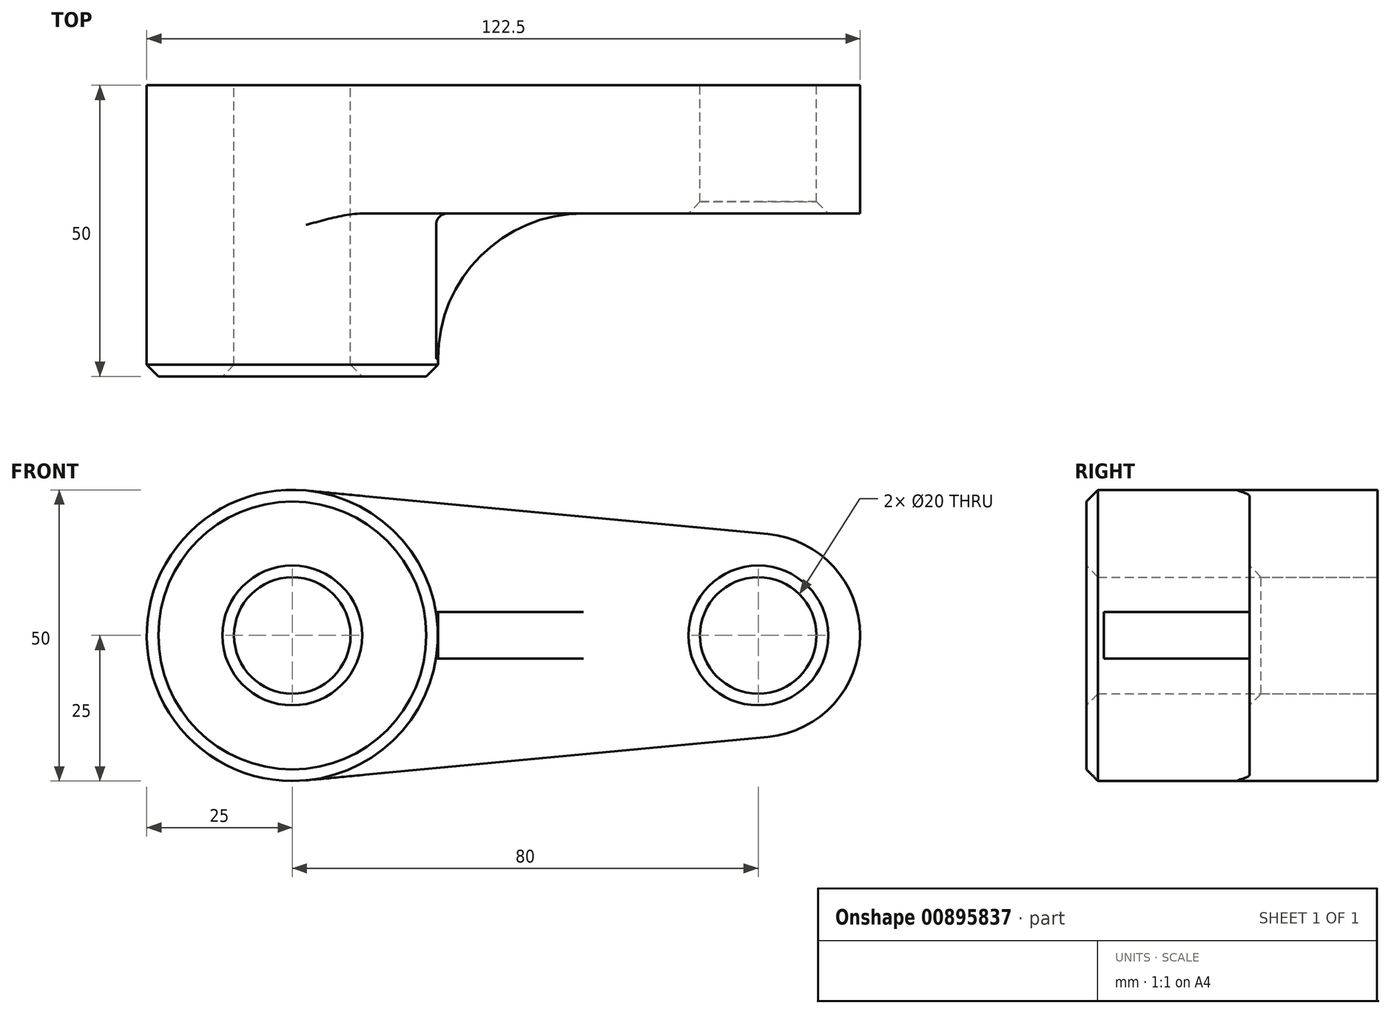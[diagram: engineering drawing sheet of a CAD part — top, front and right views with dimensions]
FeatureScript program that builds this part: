
annotation { "Feature Type Name" : "Feature", "Feature Type Description" : "" }
export const myFeature = defineFeature(function(context is Context, id is Id, definition is map)
    precondition{}
    {
        {
            var Q0;
            Q0=qCreatedBy(makeId("Front.planeOp"),FACE);
            var sketch = newSketch(context, id + "F0", { "sketchPlane" : qUnion([Q0])});
            skCircle(sketch, "E0", {"center": v(0, 0) * mm, "radius": 25 * mm});
            skCircle(sketch, "E1", {"center": v(80, 0) * mm, "radius": 17.5 * mm});
            skLineSegment(sketch, "E2", {"start": v(2.34, 24.89) * mm, "end": v(81.64, 17.42) * mm});
            skLineSegment(sketch, "E3", {"start": v(2.34, -24.89) * mm, "end": v(81.64, -17.42) * mm});
            skCircle(sketch, "E4", {"center": v(0, 0) * mm, "radius": 10 * mm});
            skCircle(sketch, "E5", {"center": v(80, 0) * mm, "radius": 10 * mm});
            skSolve(sketch);
        }
        {
            var Q0;
            Q0 = qSketchRegion(id + "F0", true);
            extrude(context, id + "F1", {"entities" : qUnion([Q0]), "depth" : 22 * mm, "offsetDistance" : 25 * mm});
        }
        {
            var Q0;
            Q0=makeQuery(id+"F0.imprint","IMPRINT",FACE,{"disambiguationData":[TD([[makeQuery(id+"F0.imprint","IMPRINT",EDGE,{"derivedFrom":sQuery(id+"F0.wireOp",EDGE,"E4")}),-1.0]])]});
            extrude(context, id + "F2", {"entities" : qUnion([Q0]), "operationType" : NewBodyOperationType.ADD, "depth" : 50 * mm, "offsetDistance" : 25 * mm});
        }
        {
            var Q0;
            Q0=makeQuery(id+"F2.opExtrude","CAP_EDGE",EDGE,{"disambiguationData":[OSD([sQuery(id+"F0.wireOp",EDGE,"E0")])],"isStart":false});
            var Q1;
            Q1=makeQuery(id+"F2.opExtrude","CAP_EDGE",EDGE,{"disambiguationData":[OSD([sQuery(id+"F0.wireOp",EDGE,"E4")])],"isStart":false});
            var Q2;
            Q2=makeQuery(id+"F1.opExtrude","CAP_EDGE",EDGE,{"disambiguationData":[OSD([sQuery(id+"F0.wireOp",EDGE,"E5")])],"isStart":false});
            chamfer(context, id + "F3", {"entities" : qUnion([Q0, Q1, Q2]), "width" : 2 * mm, "tangentPropagation" : true});
        }
        {
            var Q0;
            Q0=qCreatedBy(makeId("Top.planeOp"),FACE);
            var sketch = newSketch(context, id + "F4", { "sketchPlane" : qUnion([Q0])});
            skLineSegment(sketch, "E6", {"start": v(25, -47) * mm, "end": v(25, -48) * mm});
            skLineSegment(sketch, "E7", {"start": v(-25, -48) * mm, "end": v(-25, 0) * mm});
            skLineSegment(sketch, "E8.0", {"start": v(50, -22) * mm, "end": v(81.64, -22) * mm});
            skPoint(sketch, "E9.newPointB", {"position": v(2.34, -22) * mm});
            skArc(sketch, "E9.filletArc", {"start": v(50, -22) * mm, "mid": v(32.32, -29.32) * mm, "end": v(25, -47) * mm});
            skLineSegment(sketch, "E10", {"start": v(25, -47) * mm, "end": v(19.76, -47) * mm});
            skLineSegment(sketch, "E11", {"start": v(19.76, -47) * mm, "end": v(19.76, -16.18) * mm});
            skLineSegment(sketch, "E12", {"start": v(19.76, -16.18) * mm, "end": v(50, -16.18) * mm});
            skLineSegment(sketch, "E13", {"start": v(50, -16.18) * mm, "end": v(50, -22) * mm});
            skSolve(sketch);
        }
        {
            var Q0;
            Q0=makeQuery(id+"FmefR4HmdNPaGld_1.boolean.opBoolean","INTERSECT",EDGE,{"derivedFrom":[makeQuery(id+"F1.opExtrude","CAP_FACE",FACE,{"disambiguationData":[OSD([sQuery(id+"F0.wireOp",EDGE,"E0"),sQuery(id+"F0.wireOp",EDGE,"E1"),sQuery(id+"F0.wireOp",EDGE,"E2"),sQuery(id+"F0.wireOp",EDGE,"E3"),sQuery(id+"F0.wireOp",EDGE,"E4"),sQuery(id+"F0.wireOp",EDGE,"E5")])],"isStart":false}),makeQuery(id+"FmefR4HmdNPaGld_1.opExtrude","CAP_FACE",FACE,{"disambiguationData":[OSD([sQuery(id+"F4.wireOp",EDGE,"sk62tjqo-Fya9-pk80-HOgh-CsiJBxlOCMTc"),sQuery(id+"F4.wireOp",EDGE,"KA74Whhb-TLWN-SdVE-rRIR-7yJeO2KU4phQ"),sQuery(id+"F4.wireOp",EDGE,"j5hhdNtV-842E-OS0S-tBDo-G5zsVCp4V1sS")])],"isStart":true})]});
            var Q1;
            {var subQ0=sQuery(id+"F0.wireOp",EDGE,"E0");Q1=makeQuery(id+"FmefR4HmdNPaGld_1.boolean.opBoolean","INTERSECT",EDGE,{"derivedFrom":[makeQuery(id+"F2.boolean.opBoolean","MERGE",FACE,{"derivedFrom":[makeQuery(id+"F1.opExtrude","SWEPT_FACE",FACE,{"disambiguationData":[OSD([subQ0])]}),makeQuery(id+"F2.opExtrude","SWEPT_FACE",FACE,{"disambiguationData":[OSD([subQ0])]})]}),makeQuery(id+"FmefR4HmdNPaGld_1.opExtrude","CAP_FACE",FACE,{"disambiguationData":[OSD([sQuery(id+"F4.wireOp",EDGE,"sk62tjqo-Fya9-pk80-HOgh-CsiJBxlOCMTc"),sQuery(id+"F4.wireOp",EDGE,"KA74Whhb-TLWN-SdVE-rRIR-7yJeO2KU4phQ"),sQuery(id+"F4.wireOp",EDGE,"j5hhdNtV-842E-OS0S-tBDo-G5zsVCp4V1sS")])],"isStart":true})]});}
            var Q2;
            Q2=makeQuery(id+"FmefR4HmdNPaGld_1.boolean.opBoolean","INTERSECT",EDGE,{"derivedFrom":[makeQuery(id+"F1.opExtrude","CAP_FACE",FACE,{"disambiguationData":[OSD([sQuery(id+"F0.wireOp",EDGE,"E0"),sQuery(id+"F0.wireOp",EDGE,"E1"),sQuery(id+"F0.wireOp",EDGE,"E2"),sQuery(id+"F0.wireOp",EDGE,"E3"),sQuery(id+"F0.wireOp",EDGE,"E4"),sQuery(id+"F0.wireOp",EDGE,"E5")])],"isStart":false}),makeQuery(id+"FmefR4HmdNPaGld_1.opExtrude","CAP_FACE",FACE,{"disambiguationData":[OSD([sQuery(id+"F4.wireOp",EDGE,"sk62tjqo-Fya9-pk80-HOgh-CsiJBxlOCMTc"),sQuery(id+"F4.wireOp",EDGE,"KA74Whhb-TLWN-SdVE-rRIR-7yJeO2KU4phQ"),sQuery(id+"F4.wireOp",EDGE,"j5hhdNtV-842E-OS0S-tBDo-G5zsVCp4V1sS")])],"isStart":false})]});
            var Q3;
            {var subQ0=sQuery(id+"F0.wireOp",EDGE,"E0");Q3=makeQuery(id+"FmefR4HmdNPaGld_1.boolean.opBoolean","INTERSECT",EDGE,{"derivedFrom":[makeQuery(id+"F2.boolean.opBoolean","MERGE",FACE,{"derivedFrom":[makeQuery(id+"F1.opExtrude","SWEPT_FACE",FACE,{"disambiguationData":[OSD([subQ0])]}),makeQuery(id+"F2.opExtrude","SWEPT_FACE",FACE,{"disambiguationData":[OSD([subQ0])]})]}),makeQuery(id+"FmefR4HmdNPaGld_1.opExtrude","CAP_FACE",FACE,{"disambiguationData":[OSD([sQuery(id+"F4.wireOp",EDGE,"sk62tjqo-Fya9-pk80-HOgh-CsiJBxlOCMTc"),sQuery(id+"F4.wireOp",EDGE,"KA74Whhb-TLWN-SdVE-rRIR-7yJeO2KU4phQ"),sQuery(id+"F4.wireOp",EDGE,"j5hhdNtV-842E-OS0S-tBDo-G5zsVCp4V1sS")])],"isStart":false})]});}
            var Q4;
            {var subQ0=sQuery(id+"F0.wireOp",EDGE,"E0");var subQ1=makeQuery(id+"F2.opExtrude","SWEPT_FACE",FACE,{"disambiguationData":[OSD([subQ0])]});var subQ2=sQuery(id+"F0.wireOp",EDGE,"E2");var subQ3=makeQuery(id+"F1.opExtrude","CAP_FACE",FACE,{"disambiguationData":[OSD([subQ0,sQuery(id+"F0.wireOp",EDGE,"E1"),subQ2,sQuery(id+"F0.wireOp",EDGE,"E3"),sQuery(id+"F0.wireOp",EDGE,"E4"),sQuery(id+"F0.wireOp",EDGE,"E5")])],"isStart":false});Q4=makeQuery(id+"FmefR4HmdNPaGld_1.boolean.opBoolean","SPLIT",EDGE,{"disambiguationData":[TD([makeQuery(id+"F1.opExtrude","SWEPT_FACE",FACE,{"disambiguationData":[OSD([subQ2])]})])],"derivedFrom":makeQuery(id+"F2.boolean.opBoolean","INTERSECT",EDGE,{"derivedFrom":[subQ3,subQ1]})});}
            var Q5;
            {var subQ0=sQuery(id+"F0.wireOp",EDGE,"E0");var subQ1=makeQuery(id+"F2.opExtrude","SWEPT_FACE",FACE,{"disambiguationData":[OSD([subQ0])]});var subQ2=sQuery(id+"F0.wireOp",EDGE,"E3");var subQ3=makeQuery(id+"F1.opExtrude","CAP_FACE",FACE,{"disambiguationData":[OSD([subQ0,sQuery(id+"F0.wireOp",EDGE,"E1"),sQuery(id+"F0.wireOp",EDGE,"E2"),subQ2,sQuery(id+"F0.wireOp",EDGE,"E4"),sQuery(id+"F0.wireOp",EDGE,"E5")])],"isStart":false});Q5=makeQuery(id+"FmefR4HmdNPaGld_1.boolean.opBoolean","SPLIT",EDGE,{"disambiguationData":[TD([makeQuery(id+"F1.opExtrude","SWEPT_FACE",FACE,{"disambiguationData":[OSD([subQ2])]})])],"derivedFrom":makeQuery(id+"F2.boolean.opBoolean","INTERSECT",EDGE,{"derivedFrom":[subQ3,subQ1]})});}
            var Q6;
            Q6=makeQuery(id+"FmefR4HmdNPaGld_1.boolean.opBoolean","INTERSECT",EDGE,{"derivedFrom":[makeQuery(id+"F1.opExtrude","CAP_FACE",FACE,{"disambiguationData":[OSD([sQuery(id+"F0.wireOp",EDGE,"E0"),sQuery(id+"F0.wireOp",EDGE,"E1"),sQuery(id+"F0.wireOp",EDGE,"E2"),sQuery(id+"F0.wireOp",EDGE,"E3"),sQuery(id+"F0.wireOp",EDGE,"E4"),sQuery(id+"F0.wireOp",EDGE,"E5")])],"isStart":false}),makeQuery(id+"FmefR4HmdNPaGld_1.opExtrude","SWEPT_FACE",FACE,{"disambiguationData":[OSD([sQuery(id+"F4.wireOp",EDGE,"sk62tjqo-Fya9-pk80-HOgh-CsiJBxlOCMTc")])]})]});
            fillet(context, id + "F5", {"entities" : qUnion([Q0, Q1, Q2, Q3, Q4, Q5, Q6]), "radius" : 2 * mm, "tangentPropagation" : true, "allowEdgeOverflow" : false});
        }
        {
            var Q0;
            Q0 = qSketchRegion(id + "F4", true);
            extrude(context, id + "F6", {"entities" : qUnion([Q0]), "operationType" : NewBodyOperationType.ADD, "depth" : 4 * mm, "offsetDistance" : 25 * mm, "hasSecondDirection" : true, "secondDirectionOppositeDirection" : true, "secondDirectionDepth" : 4 * mm});
        }
    });
